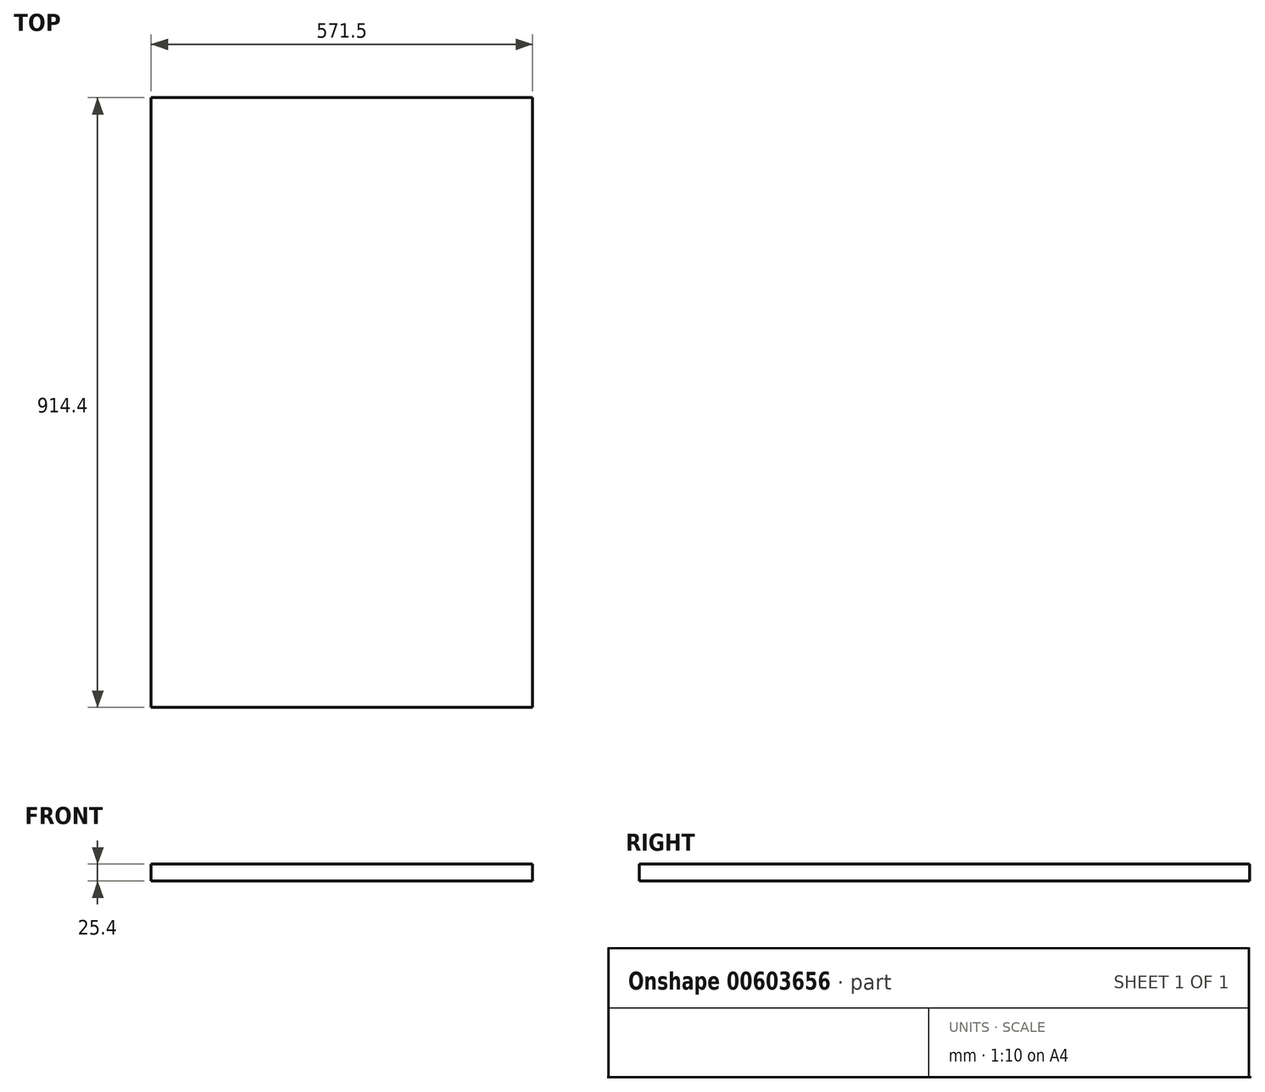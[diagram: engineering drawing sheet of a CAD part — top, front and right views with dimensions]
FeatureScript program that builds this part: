
annotation { "Feature Type Name" : "Feature", "Feature Type Description" : "" }
export const myFeature = defineFeature(function(context is Context, id is Id, definition is map)
    precondition{}
    {
        {
            var Q0;
            Q0=qCreatedBy(makeId("Top.planeOp"),FACE);
            var sketch = newSketch(context, id + "F0", { "sketchPlane" : qUnion([Q0])});
            skLineSegment(sketch, "E0.bottom", {"start": v(-125, 763.58) * mm, "end": v(446.5, 763.58) * mm});
            skLineSegment(sketch, "E0.top", {"start": v(-125, -150.82) * mm, "end": v(446.5, -150.82) * mm});
            skLineSegment(sketch, "E0.left", {"start": v(-125, 763.58) * mm, "end": v(-125, -150.82) * mm});
            skLineSegment(sketch, "E0.right", {"start": v(446.5, 763.58) * mm, "end": v(446.5, -150.82) * mm});
            skSolve(sketch);
        }
        {
            var Q0;
            Q0=makeQuery(id+"F0.imprint","IMPRINT",FACE,{"disambiguationData":[TD([[makeQuery(id+"F0.imprint","IMPRINT",EDGE,{"derivedFrom":sQuery(id+"F0.wireOp",EDGE,"E0.bottom")}),-1.0]])]});
            extrude(context, id + "F1", {"entities" : qUnion([Q0]), "depth" : 25.4 * mm, "offsetDistance" : 25.4 * mm});
        }
    });
